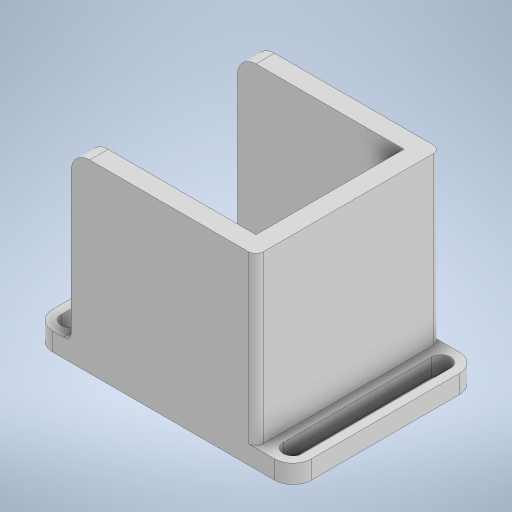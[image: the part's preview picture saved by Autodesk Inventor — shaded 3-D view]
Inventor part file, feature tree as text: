
AUTODESK INVENTOR PART (.ipt)
format: ipt  version: 2024 (Build 280153000, 153)  size: 265,728 bytes
history: native  units: mm
features: extrude x4, sketch x4, fillet x2, other x1
ambient origin geometry x8: Origin, YZ Plane, XZ Plane, XY Plane, X Axis, Y Axis, Z Axis, Center Point
bodies: Body1 (feature_tree)
feature tree (11):
  other  "ソリッド1"
  extrude  "押し出し1"  Depth=50.0mm
  extrude  "押し出し2"  Depth=50.0mm
  extrude  "押し出し4"  Depth=50.0mm TaperAngle=0.0deg
  extrude  "押し出し5"  Depth=5.0mm
  fillet  "フィレット2"  Radius=5.0mm
  fillet  "フィレット3"  Radius=5.0mm
  sketch  "スケッチ1"
  sketch  "スケッチ2"
  sketch  "スケッチ5"
  sketch  "スケッチ6"
